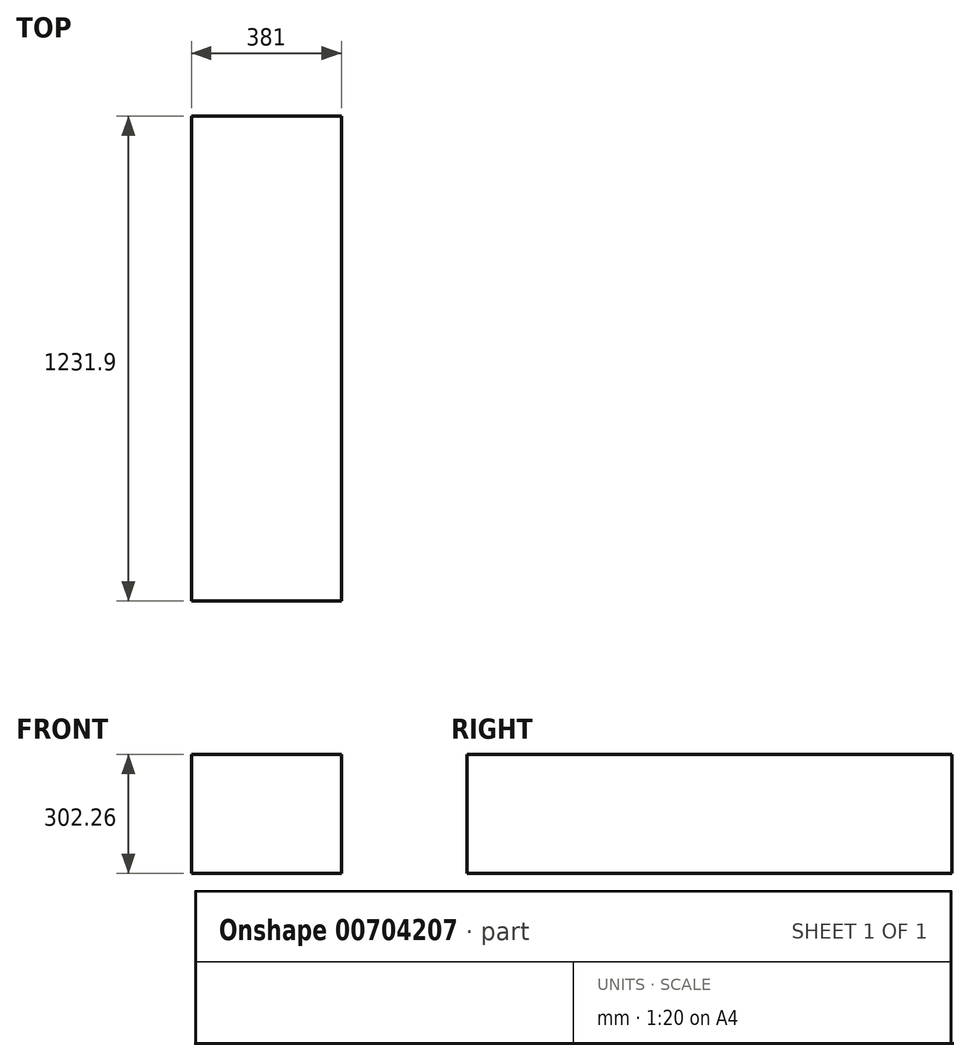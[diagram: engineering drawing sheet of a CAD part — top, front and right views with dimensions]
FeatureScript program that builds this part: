
annotation { "Feature Type Name" : "Feature", "Feature Type Description" : "" }
export const myFeature = defineFeature(function(context is Context, id is Id, definition is map)
    precondition{}
    {
        {
            var Q0;
            Q0=qCreatedBy(makeId("Top.planeOp"),FACE);
            var sketch = newSketch(context, id + "F0", { "sketchPlane" : qUnion([Q0])});
            skLineSegment(sketch, "E0.bottom", {"start": v(0, 0) * mm, "end": v(381, 0) * mm});
            skLineSegment(sketch, "E0.top", {"start": v(0, 381) * mm, "end": v(381, 381) * mm});
            skLineSegment(sketch, "E0.left", {"start": v(0, 0) * mm, "end": v(0, 381) * mm});
            skLineSegment(sketch, "E0.right", {"start": v(381, 0) * mm, "end": v(381, 381) * mm});
            skSolve(sketch);
        }
        {
            var Q0;
            Q0=makeQuery(id+"F0.imprint","IMPRINT",FACE,{"disambiguationData":[TD([[makeQuery(id+"F0.imprint","IMPRINT",EDGE,{"derivedFrom":sQuery(id+"F0.wireOp",EDGE,"E0.bottom")}),1.0]])]});
            var sketch = newSketch(context, id + "F1", { "sketchPlane" : qUnion([Q0])});
            skSolve(sketch);
        }
        {
            var Q0;
            Q0=makeQuery(id+"F1.imprint","IMPRINT",FACE,{"disambiguationData":[TD([[makeQuery(id+"F1.imprint","IMPRINT",EDGE,{"derivedFrom":makeQuery(id+"F0.imprint","IMPRINT",EDGE,{"derivedFrom":sQuery(id+"F0.wireOp",EDGE,"E0.bottom")})}),1.0]])]});
            extrude(context, id + "F2", {"entities" : qUnion([Q0]), "depth" : 302.26 * mm, "offsetDistance" : 25.4 * mm});
        }
        {
            var Q0;
            Q0=makeQuery(id+"F2.opExtrude","SWEPT_FACE",FACE,{"disambiguationData":[OSD([sQuery(id+"F0.wireOp",EDGE,"E0.bottom")])]});
            extrude(context, id + "F3", {"entities" : qUnion([Q0]), "operationType" : NewBodyOperationType.ADD, "depth" : 850.9 * mm, "offsetDistance" : 25.4 * mm});
        }
    });
